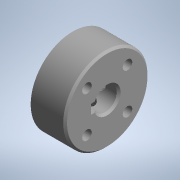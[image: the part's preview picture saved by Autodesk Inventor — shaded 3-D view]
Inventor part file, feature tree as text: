
AUTODESK INVENTOR PART (.ipt)
format: ipt  version: 2021 (Build 250183000, 183)  size: 172,544 bytes
history: native  units: mm (DEFAULTED — no unit token found)
features: other x9, sketch x8, extrude x5, revolve x3, thread x2, direct_edit x2
ambient origin geometry x8: Origin, YZ Plane, XZ Plane, XY Plane, X Axis, Y Axis, Z Axis, Center Point
bodies: Solid1 (feature_tree)
feature tree (29):
  revolve  "Revolution1"  Angle=360.0deg
  revolve  "Revolution2"  Angle=360.0deg
  thread  "Thread1"  [1 undecoded]
  revolve  "Revolution3"  [1 undecoded]
  thread  "Thread2"  [1 undecoded]
  extrude  "Extrusion1"  Depth=10.0mm TaperAngle=0.0deg
  extrude  "Extrusion2"  Depth=1.0mm
  extrude  "Extrusion3"  [1 undecoded]
  extrude  "Extrusion4"  [1 undecoded]
  extrude  "Extrusion5"  [1 undecoded]
  other  "part_XY"
  other  "part_YZ"
  other  "part_ZX"
  other  "part_X"
  other  "part_Y"
  other  "part_Z"
  other  "part_Center"
  direct_edit  "Direct Edit1"
  direct_edit  "Direct Edit3"
  sketch  "Sketch_1"  dims[d0=360.0deg d1=360.0deg]
  sketch  "Sketch_4"  dims[d13=10.0mm d14=0.0mm d15=10.0mm d16=0.0mm]
  sketch  "Sketch_3"  dims[d7=10.0mm d8=0.0mm d9=10.0mm d10=0.0mm d11=10.0mm d12=0.0mm]
  sketch  "Sketch_2"  dims[d2=7.621mm d3=0.0mm d4=360.0deg d5=7.621mm d6=0.0mm]
  sketch  "Sketch_6"  dims[d17=0.0mm d18=1.0mm]
  sketch  "Sketch_7"  dims[d20=-1.0mm]
  sketch  "Sketch_8"
  sketch  "Sketch_9"
  other  "Size1"
  other  "Size3"
note: 6 required parameter values undecoded (feature->parameter linkage not recoverable at this tier; creation-order binding heuristic only, values carry confidence <= 0.55)